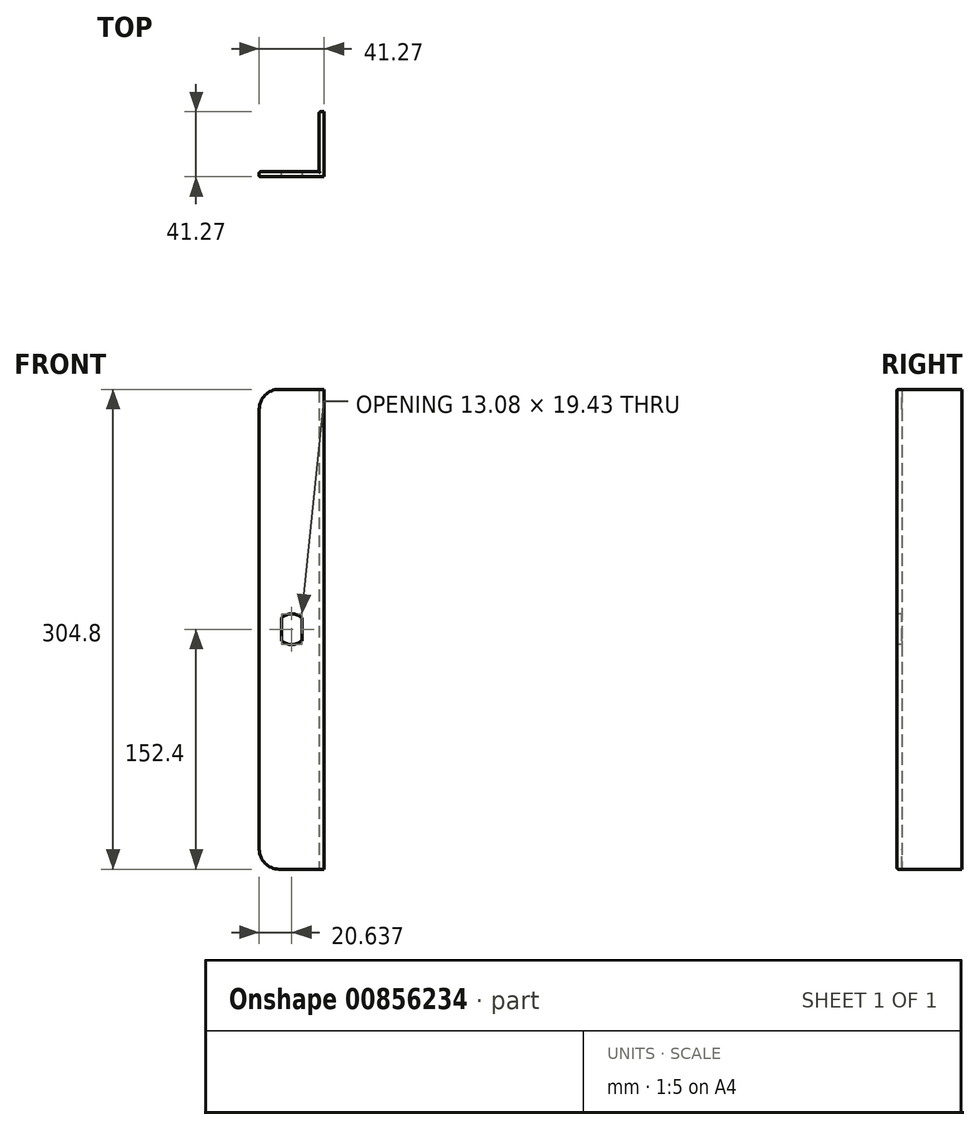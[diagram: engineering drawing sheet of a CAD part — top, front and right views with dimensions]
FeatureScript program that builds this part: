
annotation { "Feature Type Name" : "Feature", "Feature Type Description" : "" }
export const myFeature = defineFeature(function(context is Context, id is Id, definition is map)
    precondition{}
    {
        {
            var Q0;
            Q0=qCreatedBy(makeId("Top.planeOp"),FACE);
            var sketch = newSketch(context, id + "F0", { "sketchPlane" : qUnion([Q0])});
            skLineSegment(sketch, "E0", {"start": v(0, 0) * mm, "end": v(41.28, 0) * mm});
            skLineSegment(sketch, "E1", {"start": v(41.28, 0) * mm, "end": v(41.27, 41.28) * mm});
            skLineSegment(sketch, "E2.0", {"start": v(38.1, 3.18) * mm, "end": v(38.1, 41.28) * mm});
            skLineSegment(sketch, "E2.1", {"start": v(0, 3.18) * mm, "end": v(38.1, 3.18) * mm});
            skLineSegment(sketch, "E3", {"start": v(41.27, 41.28) * mm, "end": v(38.1, 41.28) * mm});
            skLineSegment(sketch, "E4", {"start": v(0, 3.18) * mm, "end": v(0, 0) * mm});
            skSolve(sketch);
        }
        {
            var Q0;
            Q0 = qSketchRegion(id + "F0", true);
            extrude(context, id + "F1", {"entities" : qUnion([Q0]), "depth" : 304.8 * mm, "offsetDistance" : 25.4 * mm});
        }
        {
            var Q0;
            Q0=makeQuery(id+"F1.opExtrude","SWEPT_EDGE",EDGE,{"disambiguationData":[OSD([sQuery(id+"F0.wireOp",EDGE,"E0"),sQuery(id+"F0.wireOp",EDGE,"E4")])]});
            var Q1;
            Q1=makeQuery(id+"F1.opExtrude","CAP_EDGE",EDGE,{"disambiguationData":[OSD([sQuery(id+"F0.wireOp",EDGE,"E0")])],"isStart":false});
            var Q2;
            Q2=makeQuery(id+"F1.opExtrude","CAP_EDGE",EDGE,{"disambiguationData":[OSD([sQuery(id+"F0.wireOp",EDGE,"E0")])],"isStart":true});
            var Q3;
            Q3=makeQuery(id+"F1.opExtrude","CAP_EDGE",EDGE,{"disambiguationData":[OSD([sQuery(id+"F0.wireOp",EDGE,"E2.0")])],"isStart":false});
            var Q4;
            Q4=makeQuery(id+"F1.opExtrude","CAP_EDGE",EDGE,{"disambiguationData":[OSD([sQuery(id+"F0.wireOp",EDGE,"E2.1")])],"isStart":false});
            var Q5;
            Q5=makeQuery(id+"F1.opExtrude","SWEPT_EDGE",EDGE,{"disambiguationData":[OSD([sQuery(id+"F0.wireOp",EDGE,"E2.1"),sQuery(id+"F0.wireOp",EDGE,"E4")])]});
            var Q6;
            Q6=makeQuery(id+"F1.opExtrude","CAP_EDGE",EDGE,{"disambiguationData":[OSD([sQuery(id+"F0.wireOp",EDGE,"E2.1")])],"isStart":true});
            var Q7;
            Q7=makeQuery(id+"F1.opExtrude","CAP_EDGE",EDGE,{"disambiguationData":[OSD([sQuery(id+"F0.wireOp",EDGE,"E2.0")])],"isStart":true});
            var Q8;
            Q8=makeQuery(id+"F1.opExtrude","SWEPT_EDGE",EDGE,{"disambiguationData":[OSD([sQuery(id+"F0.wireOp",EDGE,"E2.0"),sQuery(id+"F0.wireOp",EDGE,"E3")])]});
            fillet(context, id + "F2", {"entities" : qUnion([Q0, Q1, Q2, Q3, Q4, Q5, Q6, Q7, Q8]), "radius" : 0.76 * mm, "tangentPropagation" : true, "allowEdgeOverflow" : false});
        }
        {
            var Q0;
            Q0=qCreatedBy(makeId("Top.planeOp"),FACE);
            cPlane(context, id + "F3", {"entities" : qUnion([Q0]), "cplaneType" : CPlaneType.OFFSET, "offset" : 152.4 * mm, "width" : 152.4 * mm, "height" : 152.4 * mm});
        }
        {
            var Q0;
            Q0=makeQuery(id+"F1.opExtrude","SWEPT_FACE",FACE,{"disambiguationData":[OSD([sQuery(id+"F0.wireOp",EDGE,"E0")])]});
            var sketch = newSketch(context, id + "F4", { "sketchPlane" : qUnion([Q0])});
            skPoint(sketch, "E5", {"position": v(20.64, 152.4) * mm});
            skCircle(sketch, "E6", {"center": v(20.64, 152.4) * mm, "radius": 9.72 * mm, "construction": true});
            skLineSegment(sketch, "E7", {"start": v(20.64, 152.4) * mm, "end": v(20.64, 161.33) * mm, "construction": true});
            skLineSegment(sketch, "E8", {"start": v(14.1, 159.58) * mm, "end": v(14.1, 145.22) * mm});
            skLineSegment(sketch, "E9", {"start": v(27.18, 159.58) * mm, "end": v(27.18, 145.22) * mm});
            skArc(sketch, "E10", {"start": v(14.1, 145.22) * mm, "mid": v(20.64, 142.68) * mm, "end": v(27.18, 145.22) * mm});
            skArc(sketch, "E11", {"start": v(14.1, 159.58) * mm, "mid": v(20.64, 162.12) * mm, "end": v(27.18, 159.58) * mm});
            skSolve(sketch);
        }
        {
            var Q0;
            Q0 = qSketchRegion(id + "F4", true);
            extrude(context, id + "F5", {"entities" : qUnion([Q0]), "operationType" : NewBodyOperationType.REMOVE, "oppositeDirection" : true, "depth" : 25.4 * mm, "offsetDistance" : 25.4 * mm});
        }
        {
            var Q0;
            Q0=makeQuery(id+"F5.boolean.opBoolean","COPY",EDGE,{"derivedFrom":makeQuery(id+"F5.opExtrude","SWEPT_EDGE",EDGE,{"disambiguationData":[OSD([sQuery(id+"F4.wireOp",EDGE,"E8"),sQuery(id+"F4.wireOp",EDGE,"E10")])]})});
            var Q1;
            Q1=makeQuery(id+"F5.boolean.opBoolean","COPY",EDGE,{"derivedFrom":makeQuery(id+"F5.opExtrude","SWEPT_EDGE",EDGE,{"disambiguationData":[OSD([sQuery(id+"F4.wireOp",EDGE,"E8"),sQuery(id+"F4.wireOp",EDGE,"E11")])]})});
            var Q2;
            Q2=makeQuery(id+"F5.boolean.opBoolean","COPY",EDGE,{"derivedFrom":makeQuery(id+"F5.opExtrude","SWEPT_EDGE",EDGE,{"disambiguationData":[OSD([sQuery(id+"F4.wireOp",EDGE,"E9"),sQuery(id+"F4.wireOp",EDGE,"E11")])]})});
            var Q3;
            Q3=makeQuery(id+"F5.boolean.opBoolean","COPY",EDGE,{"derivedFrom":makeQuery(id+"F5.opExtrude","SWEPT_EDGE",EDGE,{"disambiguationData":[OSD([sQuery(id+"F4.wireOp",EDGE,"E9"),sQuery(id+"F4.wireOp",EDGE,"E10")])]})});
            fillet(context, id + "F6", {"entities" : qUnion([Q0, Q1, Q2, Q3]), "radius" : 0.38 * mm, "tangentPropagation" : true, "allowEdgeOverflow" : false});
        }
        {
            var Q0;
            Q0=makeQuery(id+"F1.opExtrude","CAP_EDGE",EDGE,{"disambiguationData":[OSD([sQuery(id+"F0.wireOp",EDGE,"E4")])],"isStart":false});
            var Q1;
            Q1=makeQuery(id+"F1.opExtrude","CAP_EDGE",EDGE,{"disambiguationData":[OSD([sQuery(id+"F0.wireOp",EDGE,"E4")])],"isStart":true});
            fillet(context, id + "F7", {"entities" : qUnion([Q0, Q1]), "radius" : 12.7 * mm, "tangentPropagation" : true, "allowEdgeOverflow" : false});
        }
    });
